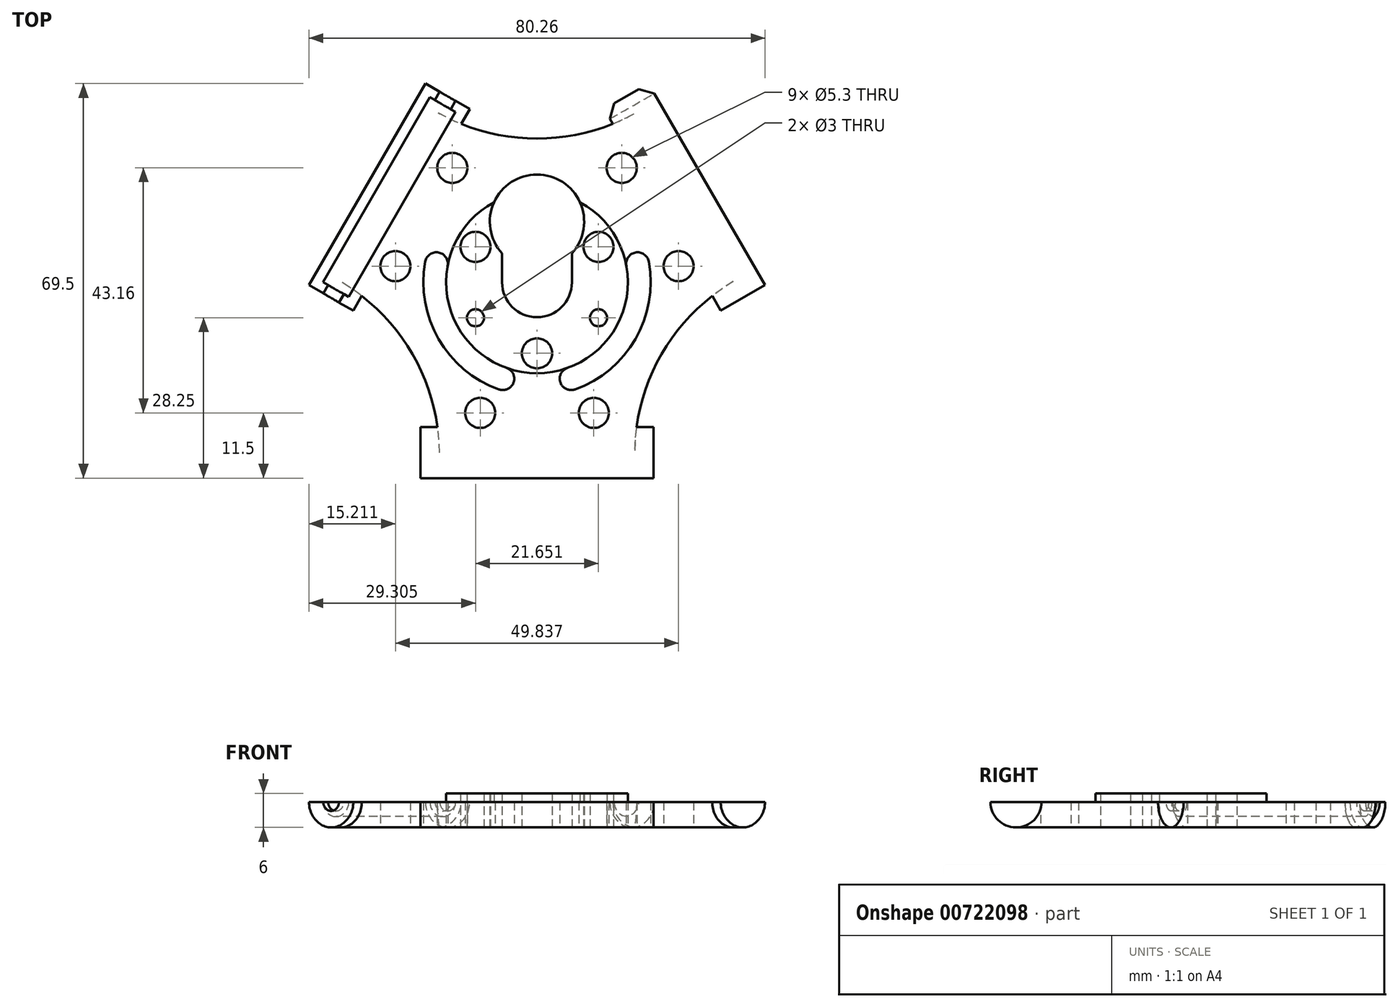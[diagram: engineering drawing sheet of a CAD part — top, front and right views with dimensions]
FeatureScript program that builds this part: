
annotation { "Feature Type Name" : "Feature", "Feature Type Description" : "" }
export const myFeature = defineFeature(function(context is Context, id is Id, definition is map)
    precondition{}
    {
        {
            var Q0;
            Q0=qCreatedBy(makeId("Top.planeOp"),FACE);
            var sketch = newSketch(context, id + "F0", { "sketchPlane" : qUnion([Q0])});
            skArc(sketch, "E0", {"start": v(-6.15, 0) * mm, "mid": v(0, -6.15) * mm, "end": v(6.15, 0) * mm});
            skArc(sketch, "E1", {"start": v(6.15, 5.12) * mm, "mid": v(0, 19) * mm, "end": v(-6.15, 5.12) * mm});
            skLineSegment(sketch, "E2", {"start": v(6.15, 0) * mm, "end": v(6.15, 5.12) * mm});
            skLineSegment(sketch, "E3", {"start": v(-6.15, 0) * mm, "end": v(-6.15, 5.12) * mm});
            skLineSegment(sketch, "E4", {"start": v(-32.33, -5) * mm, "end": v(-30.83, -2.4) * mm});
            skLineSegment(sketch, "E5", {"start": v(-11.83, 30.5) * mm, "end": v(-19.63, 35) * mm});
            skLineSegment(sketch, "E6", {"start": v(-19.63, 35) * mm, "end": v(-40.13, -0.5) * mm});
            skLineSegment(sketch, "E7", {"start": v(-40.13, -0.5) * mm, "end": v(-32.33, -5) * mm});
            skLineSegment(sketch, "E8", {"start": v(-36.23, -2.75) * mm, "end": v(-15.73, 32.75) * mm, "construction": true});
            skLineSegment(sketch, "E9", {"start": v(-25.98, 15) * mm, "end": v(0, 0) * mm, "construction": true});
            skCircle(sketch, "E10", {"center": v(0, 0) * mm, "radius": 8 * mm, "construction": true});
            skLineSegment(sketch, "E11.1.0", {"start": v(20.5, -25.5) * mm, "end": v(17.5, -25.5) * mm});
            skLineSegment(sketch, "E11.1.1", {"start": v(-20.5, -25.5) * mm, "end": v(-20.5, -34.5) * mm});
            skLineSegment(sketch, "E11.1.2", {"start": v(-20.5, -34.5) * mm, "end": v(20.5, -34.5) * mm});
            skLineSegment(sketch, "E11.1.3", {"start": v(20.5, -34.5) * mm, "end": v(20.5, -25.5) * mm});
            skLineSegment(sketch, "E11.1.4", {"start": v(0, -30) * mm, "end": v(0, 0) * mm, "construction": true});
            skLineSegment(sketch, "E11.1.5", {"start": v(20.5, -30) * mm, "end": v(-20.5, -30) * mm, "construction": true});
            skLineSegment(sketch, "E11.2.0", {"start": v(11.83, 30.5) * mm, "end": v(13.33, 27.9) * mm});
            skLineSegment(sketch, "E11.2.1", {"start": v(32.33, -5) * mm, "end": v(40.13, -0.5) * mm});
            skLineSegment(sketch, "E11.2.2", {"start": v(40.13, -0.5) * mm, "end": v(19.63, 35) * mm});
            skLineSegment(sketch, "E11.2.3", {"start": v(19.63, 35) * mm, "end": v(11.83, 30.5) * mm});
            skLineSegment(sketch, "E11.2.4", {"start": v(25.98, 15) * mm, "end": v(0, 0) * mm, "construction": true});
            skLineSegment(sketch, "E11.2.5", {"start": v(15.73, 32.75) * mm, "end": v(36.23, -2.75) * mm, "construction": true});
            skArc(sketch, "E12", {"start": v(-13.33, 27.9) * mm, "mid": v(0, 25.3) * mm, "end": v(13.33, 27.9) * mm});
            skArc(sketch, "E13.1.0", {"start": v(-17.5, -25.5) * mm, "mid": v(-21.92, -12.65) * mm, "end": v(-30.83, -2.4) * mm});
            skArc(sketch, "E13.2.0", {"start": v(30.83, -2.4) * mm, "mid": v(21.92, -12.65) * mm, "end": v(17.5, -25.5) * mm});
            skLineSegment(sketch, "E14.trimOffspring", {"start": v(-13.33, 27.9) * mm, "end": v(-11.83, 30.5) * mm});
            skLineSegment(sketch, "E15.trimOffspring", {"start": v(-17.5, -25.5) * mm, "end": v(-20.5, -25.5) * mm});
            skLineSegment(sketch, "E16.trimOffspring", {"start": v(30.83, -2.4) * mm, "end": v(32.33, -5) * mm});
            skCircle(sketch, "E17", {"center": v(0, -12.5) * mm, "radius": 2.65 * mm});
            skCircle(sketch, "E18.2.0", {"center": v(10.83, 6.25) * mm, "radius": 2.65 * mm});
            skCircle(sketch, "E18.4.0", {"center": v(-10.83, 6.25) * mm, "radius": 2.65 * mm});
            skCircle(sketch, "E18.5.0", {"center": v(-10.83, -6.25) * mm, "radius": 1.5 * mm});
            skCircle(sketch, "E19", {"center": v(-24.92, 2.84) * mm, "radius": 2.65 * mm});
            skCircle(sketch, "E20.MirrorC", {"center": v(-14.92, 20.16) * mm, "radius": 2.65 * mm});
            skArc(sketch, "E21", {"start": v(-15.73, 2.92) * mm, "mid": v(-13.86, -8) * mm, "end": v(-5.33, -15.08) * mm});
            skCircle(sketch, "E22.1.0", {"center": v(10, -23) * mm, "radius": 2.65 * mm});
            skCircle(sketch, "E22.1.1", {"center": v(-10, -23) * mm, "radius": 2.65 * mm});
            skCircle(sketch, "E22.2.0", {"center": v(14.92, 20.16) * mm, "radius": 2.65 * mm});
            skCircle(sketch, "E22.2.1", {"center": v(24.92, 2.84) * mm, "radius": 2.65 * mm});
            skArc(sketch, "E23", {"start": v(-19.66, 3.65) * mm, "mid": v(-17.32, -10) * mm, "end": v(-6.67, -18.86) * mm});
            skArc(sketch, "E24", {"start": v(-15.73, 2.92) * mm, "mid": v(-17.33, 5.26) * mm, "end": v(-19.66, 3.65) * mm});
            skArc(sketch, "E25", {"start": v(-6.67, -18.86) * mm, "mid": v(-4.11, -17.64) * mm, "end": v(-5.33, -15.08) * mm});
            skArc(sketch, "E26.MirrorCS", {"start": v(15.73, 2.92) * mm, "mid": v(13.86, -8) * mm, "end": v(5.33, -15.08) * mm});
            skArc(sketch, "E27.MirrorCS", {"start": v(19.66, 3.65) * mm, "mid": v(17.32, -10) * mm, "end": v(6.67, -18.86) * mm});
            skArc(sketch, "E28.MirrorCS", {"start": v(15.73, 2.92) * mm, "mid": v(17.33, 5.26) * mm, "end": v(19.66, 3.65) * mm});
            skArc(sketch, "E29.MirrorCS", {"start": v(6.67, -18.86) * mm, "mid": v(4.11, -17.64) * mm, "end": v(5.33, -15.08) * mm});
            skLineSegment(sketch, "E30", {"start": v(-10.83, -6.25) * mm, "end": v(0, 0) * mm, "construction": true});
            skCircle(sketch, "E31", {"center": v(0, 0) * mm, "radius": 12.5 * mm, "construction": true});
            skCircle(sketch, "E32.MirrorC", {"center": v(10.83, -6.25) * mm, "radius": 1.5 * mm});
            skSolve(sketch);
        }
        {
            var Q0;
            Q0 = qSketchRegion(id + "F0", true);
            extrude(context, id + "F1", {"entities" : qUnion([Q0]), "depth" : 4.5 * mm, "offsetDistance" : 25 * mm});
        }
        {
            var Q0;
            Q0=makeQuery(id+"F1.opExtrude","SWEPT_FACE",FACE,{"disambiguationData":[OSD([sQuery(id+"F0.wireOp",EDGE,"E7")])]});
            var sketch = newSketch(context, id + "F2", { "sketchPlane" : qUnion([Q0])});
            skCircle(sketch, "E33", {"center": v(-30, 4.5) * mm, "radius": 1.6 * mm});
            skSolve(sketch);
        }
        {
            var Q0;
            Q0 = qSketchRegion(id + "F2", true);
            extrude(context, id + "F3", {"entities" : qUnion([Q0]), "operationType" : NewBodyOperationType.REMOVE, "endBound" : BoundingType.THROUGH_ALL, "oppositeDirection" : true, "depth" : 25 * mm, "offsetDistance" : 25 * mm});
        }
        {
            var Q0;
            Q0=makeQuery(id+"F1.opExtrude","SWEPT_FACE",FACE,{"disambiguationData":[OSD([sQuery(id+"F0.wireOp",EDGE,"E7")])]});
            var Q1;
            Q1=qCreatedBy(makeId("Origin.pointOp"),VERTEX);
            cPlane(context, id + "F4", {"entities" : qUnion([Q0, Q1]), "cplaneType" : CPlaneType.PLANE_POINT, "offset" : 25 * mm, "width" : 150 * mm, "height" : 150 * mm});
        }
        {
            var Q0;
            Q0=qCreatedBy(id+"F4.planeOp",FACE);
            var sketch = newSketch(context, id + "F5", { "sketchPlane" : qUnion([Q0])});
            skArc(sketch, "E34", {"start": v(-31.6, 4.5) * mm, "mid": v(-30, 2.9) * mm, "end": v(-28.4, 4.5) * mm, "construction": true});
            skCircle(sketch, "E35", {"center": v(-30, 4.5) * mm, "radius": 2.6 * mm});
            skSolve(sketch);
        }
        {
            var Q0;
            Q0 = qSketchRegion(id + "F5", true);
            extrude(context, id + "F6", {"entities" : qUnion([Q0]), "operationType" : NewBodyOperationType.REMOVE, "oppositeDirection" : true, "depth" : 18.8 * mm, "offsetDistance" : 25 * mm, "hasSecondDirection" : true, "secondDirectionOppositeDirection" : false, "secondDirectionDepth" : 18.8 * mm});
        }
        {
            var Q0;
            Q0=qCreatedBy(makeId("Front.planeOp"),FACE);
            var sketch = newSketch(context, id + "F7", { "sketchPlane" : qUnion([Q0])});
            skLineSegment(sketch, "E36", {"start": v(0, 0) * mm, "end": v(0, 59.84) * mm, "construction": true});
            skSolve(sketch);
        }
        {
            var Q0;
            Q0=makeQuery(id+"F1.opExtrude","CAP_EDGE",EDGE,{"disambiguationData":[OSD([sQuery(id+"F0.wireOp",EDGE,"E4")])],"isStart":true});
            var Q1;
            Q1=makeQuery(id+"F1.opExtrude","CAP_EDGE",EDGE,{"disambiguationData":[OSD([sQuery(id+"F0.wireOp",EDGE,"E6")])],"isStart":true});
            var Q2;
            Q2=makeQuery(id+"F1.opExtrude","CAP_EDGE",EDGE,{"disambiguationData":[OSD([sQuery(id+"F0.wireOp",EDGE,"E14.trimOffspring")])],"isStart":true});
            var Q3;
            Q3=makeQuery(id+"F1.opExtrude","CAP_EDGE",EDGE,{"disambiguationData":[OSD([sQuery(id+"F0.wireOp",EDGE,"E15.trimOffspring")])],"isStart":true});
            var Q4;
            Q4=makeQuery(id+"F1.opExtrude","CAP_EDGE",EDGE,{"disambiguationData":[OSD([sQuery(id+"F0.wireOp",EDGE,"E11.1.2")])],"isStart":true});
            var Q5;
            Q5=makeQuery(id+"F1.opExtrude","CAP_EDGE",EDGE,{"disambiguationData":[OSD([sQuery(id+"F0.wireOp",EDGE,"E11.1.0")])],"isStart":true});
            var Q6;
            Q6=makeQuery(id+"F1.opExtrude","CAP_EDGE",EDGE,{"disambiguationData":[OSD([sQuery(id+"F0.wireOp",EDGE,"E16.trimOffspring")])],"isStart":true});
            var Q7;
            Q7=makeQuery(id+"F1.opExtrude","CAP_EDGE",EDGE,{"disambiguationData":[OSD([sQuery(id+"F0.wireOp",EDGE,"E11.2.2")])],"isStart":true});
            var Q8;
            Q8=makeQuery(id+"F1.opExtrude","CAP_EDGE",EDGE,{"disambiguationData":[OSD([sQuery(id+"F0.wireOp",EDGE,"E11.2.0")])],"isStart":true});
            fillet(context, id + "F8", {"entities" : qUnion([Q0, Q1, Q2, Q3, Q4, Q5, Q6, Q7, Q8]), "radius" : 4.5 * mm, "tangentPropagation" : true, "allowEdgeOverflow" : false});
        }
        {
            var Q0;
            Q0=makeQuery(id+"F8.opFillet","BLEND_EDGE",EDGE,{"blendedFrom":[makeQuery(id+"F1.opExtrude","CAP_EDGE",EDGE,{"disambiguationData":[OSD([sQuery(id+"F0.wireOp",EDGE,"E6")])],"isStart":true}),makeQuery(id+"F1.opExtrude","SWEPT_FACE",FACE,{"disambiguationData":[OSD([sQuery(id+"F0.wireOp",EDGE,"E7")])]})],"blendedInto":[makeQuery(id+"F1.opExtrude","SWEPT_FACE",FACE,{"disambiguationData":[OSD([sQuery(id+"F0.wireOp",EDGE,"E7")])]})]});
            var Q1;
            Q1=makeQuery(id+"F8.opFillet","BLEND_EDGE",EDGE,{"blendedFrom":[makeQuery(id+"F1.opExtrude","CAP_EDGE",EDGE,{"disambiguationData":[OSD([sQuery(id+"F0.wireOp",EDGE,"E14.trimOffspring")])],"isStart":true}),makeQuery(id+"F1.opExtrude","SWEPT_FACE",FACE,{"disambiguationData":[OSD([sQuery(id+"F0.wireOp",EDGE,"E5")])]})],"blendedInto":[makeQuery(id+"F1.opExtrude","SWEPT_FACE",FACE,{"disambiguationData":[OSD([sQuery(id+"F0.wireOp",EDGE,"E5")])]})]});
            var Q2;
            Q2=makeQuery(id+"F8.opFillet","BLEND_EDGE",EDGE,{"blendedFrom":[makeQuery(id+"F1.opExtrude","CAP_EDGE",EDGE,{"disambiguationData":[OSD([sQuery(id+"F0.wireOp",EDGE,"E11.2.0")])],"isStart":true}),makeQuery(id+"F1.opExtrude","SWEPT_FACE",FACE,{"disambiguationData":[OSD([sQuery(id+"F0.wireOp",EDGE,"E11.2.3")])]})],"blendedInto":[makeQuery(id+"F1.opExtrude","SWEPT_FACE",FACE,{"disambiguationData":[OSD([sQuery(id+"F0.wireOp",EDGE,"E11.2.3")])]})]});
            var Q3;
            Q3=makeQuery(id+"F8.opFillet","BLEND_EDGE",EDGE,{"blendedFrom":[makeQuery(id+"F1.opExtrude","CAP_EDGE",EDGE,{"disambiguationData":[OSD([sQuery(id+"F0.wireOp",EDGE,"E15.trimOffspring")])],"isStart":true}),makeQuery(id+"F1.opExtrude","SWEPT_FACE",FACE,{"disambiguationData":[OSD([sQuery(id+"F0.wireOp",EDGE,"E11.1.1")])]})],"blendedInto":[makeQuery(id+"F1.opExtrude","SWEPT_FACE",FACE,{"disambiguationData":[OSD([sQuery(id+"F0.wireOp",EDGE,"E11.1.1")])]})]});
            var Q4;
            Q4=makeQuery(id+"F8.opFillet","BLEND_EDGE",EDGE,{"blendedFrom":[makeQuery(id+"F1.opExtrude","CAP_EDGE",EDGE,{"disambiguationData":[OSD([sQuery(id+"F0.wireOp",EDGE,"E11.1.2")])],"isStart":true}),makeQuery(id+"F1.opExtrude","SWEPT_FACE",FACE,{"disambiguationData":[OSD([sQuery(id+"F0.wireOp",EDGE,"E11.1.3")])]})],"blendedInto":[makeQuery(id+"F1.opExtrude","SWEPT_FACE",FACE,{"disambiguationData":[OSD([sQuery(id+"F0.wireOp",EDGE,"E11.1.3")])]})]});
            var Q5;
            Q5=makeQuery(id+"F8.opFillet","BLEND_EDGE",EDGE,{"blendedFrom":[makeQuery(id+"F1.opExtrude","CAP_EDGE",EDGE,{"disambiguationData":[OSD([sQuery(id+"F0.wireOp",EDGE,"E16.trimOffspring")])],"isStart":true}),makeQuery(id+"F1.opExtrude","SWEPT_FACE",FACE,{"disambiguationData":[OSD([sQuery(id+"F0.wireOp",EDGE,"E11.2.1")])]})],"blendedInto":[makeQuery(id+"F1.opExtrude","SWEPT_FACE",FACE,{"disambiguationData":[OSD([sQuery(id+"F0.wireOp",EDGE,"E11.2.1")])]})]});
            chamfer(context, id + "F9", {"entities" : qUnion([Q0, Q1, Q2, Q3, Q4, Q5]), "width" : 2 * mm, "tangentPropagation" : true});
        }
        {
            var Q0;
            {var subQ0=sQuery(id+"F0.wireOp",EDGE,"E29.MirrorCS");var subQ2=sQuery(id+"F0.wireOp",EDGE,"E28.MirrorCS");var subQ4=sQuery(id+"F0.wireOp",EDGE,"E27.MirrorCS");var subQ8=sQuery(id+"F0.wireOp",EDGE,"E26.MirrorCS");var subQ11=sQuery(id+"F0.wireOp",EDGE,"E25");var subQ14=sQuery(id+"F0.wireOp",EDGE,"E24");var subQ16=sQuery(id+"F0.wireOp",EDGE,"E23");var subQ18=sQuery(id+"F0.wireOp",EDGE,"E22.2.1");var subQ20=sQuery(id+"F0.wireOp",EDGE,"E22.2.0");var subQ22=sQuery(id+"F0.wireOp",EDGE,"E22.1.1");var subQ24=sQuery(id+"F0.wireOp",EDGE,"E22.1.0");var subQ26=sQuery(id+"F0.wireOp",EDGE,"E21");var subQ28=sQuery(id+"F0.wireOp",EDGE,"E20.MirrorC");var subQ30=sQuery(id+"F0.wireOp",EDGE,"E19");var subQ32=sQuery(id+"F0.wireOp",EDGE,"E18.5.0");var subQ34=sQuery(id+"F0.wireOp",EDGE,"E18.4.0");var subQ36=sQuery(id+"F0.wireOp",EDGE,"E11.1.3");var subQ38=sQuery(id+"F0.wireOp",EDGE,"E11.1.0");var subQ40=sQuery(id+"F0.wireOp",EDGE,"E7");var subQ42=sQuery(id+"F0.wireOp",EDGE,"E5");var subQ47=sQuery(id+"F0.wireOp",EDGE,"E17");var subQ49=sQuery(id+"F0.wireOp",EDGE,"E4");var subQ51=sQuery(id+"F0.wireOp",EDGE,"E11.1.1");var subQ53=sQuery(id+"F0.wireOp",EDGE,"E0");var subQ54=makeQuery(id+"F1.opExtrude","SWEPT_FACE",FACE,{"disambiguationData":[OSD([subQ53])]});var subQ55=sQuery(id+"F0.wireOp",EDGE,"E16.trimOffspring");var subQ57=sQuery(id+"F0.wireOp",EDGE,"E3");var subQ59=sQuery(id+"F0.wireOp",EDGE,"E1");var subQ61=sQuery(id+"F0.wireOp",EDGE,"E18.2.0");var subQ63=sQuery(id+"F0.wireOp",EDGE,"E2");var subQ65=sQuery(id+"F0.wireOp",EDGE,"E11.2.0");var subQ67=sQuery(id+"F0.wireOp",EDGE,"E11.2.1");var subQ69=sQuery(id+"F0.wireOp",EDGE,"E11.2.3");var subQ72=sQuery(id+"F0.wireOp",EDGE,"E12");var subQ74=sQuery(id+"F0.wireOp",EDGE,"E13.1.0");var subQ76=sQuery(id+"F0.wireOp",EDGE,"E13.2.0");var subQ78=sQuery(id+"F0.wireOp",EDGE,"E14.trimOffspring");var subQ80=sQuery(id+"F0.wireOp",EDGE,"E15.trimOffspring");var subQ82=sQuery(id+"F0.wireOp",EDGE,"E18.1.0");var subQ84=sQuery(id+"F0.wireOp",EDGE,"E11.2.2");var subQ86=sQuery(id+"F0.wireOp",EDGE,"E11.1.2");Q0=makeQuery(id+"Fxi4iVRiwFdOaLl_1.2.F3.boolean.opBoolean","SPLIT",FACE,{"disambiguationData":[TD([subQ54])],"derivedFrom":makeQuery(id+"Fxi4iVRiwFdOaLl_1.1.F3.boolean.opBoolean","SPLIT",FACE,{"disambiguationData":[TD([subQ54])],"derivedFrom":makeQuery(id+"F3.boolean.opBoolean","SPLIT",FACE,{"disambiguationData":[TD([subQ54])],"derivedFrom":makeQuery(id+"F1.opExtrude","CAP_FACE",FACE,{"disambiguationData":[OSD([subQ53,subQ59,subQ63,subQ57,subQ49,subQ42,sQuery(id+"F0.wireOp",EDGE,"E6"),subQ40,subQ38,subQ51,subQ86,subQ36,subQ65,subQ67,subQ84,subQ69,subQ72,subQ74,subQ76,subQ78,subQ80,subQ55,subQ47,subQ82,subQ61,subQ34,subQ32,subQ30,subQ28,subQ26,subQ24,subQ22,subQ20,subQ18,subQ16,subQ14,subQ11,subQ8,subQ4,subQ2,subQ0])],"isStart":false})})})});}
            var sketch = newSketch(context, id + "F10", { "sketchPlane" : qUnion([Q0])});
            skArc(sketch, "E37", {"start": v(-7.57, 14.1) * mm, "mid": v(0, -16) * mm, "end": v(7.57, 14.1) * mm});
            skArc(sketch, "E38.0", {"start": v(6.15, 5.12) * mm, "mid": v(8.2, 9.4) * mm, "end": v(7.57, 14.1) * mm});
            skLineSegment(sketch, "E39.0", {"start": v(-6.15, 0) * mm, "end": v(-6.15, 5.12) * mm});
            skArc(sketch, "E40.0", {"start": v(-6.15, 0) * mm, "mid": v(0, -6.15) * mm, "end": v(6.15, 0) * mm});
            skLineSegment(sketch, "E41.0", {"start": v(6.15, 0) * mm, "end": v(6.15, 5.12) * mm});
            skCircle(sketch, "E42.0", {"center": v(10.83, 6.25) * mm, "radius": 2.65 * mm});
            skCircle(sketch, "E43.0", {"center": v(0, -12.5) * mm, "radius": 2.65 * mm});
            skCircle(sketch, "E44.0", {"center": v(-10.83, -6.25) * mm, "radius": 1.5 * mm});
            skCircle(sketch, "E45.0", {"center": v(-10.83, 6.25) * mm, "radius": 2.65 * mm});
            skArc(sketch, "E46.trimOffspring", {"start": v(-7.57, 14.1) * mm, "mid": v(-8.2, 9.4) * mm, "end": v(-6.15, 5.12) * mm});
            skCircle(sketch, "E47.0", {"center": v(10.83, -6.25) * mm, "radius": 1.5 * mm});
            skSolve(sketch);
        }
        {
            var Q0;
            Q0 = qSketchRegion(id + "F10", true);
            var Q1;
            Q1=makeQuery(id+"F1.opExtrude","CAP_FACE",FACE,{"disambiguationData":[OSD([sQuery(id+"F0.wireOp",EDGE,"E0"),sQuery(id+"F0.wireOp",EDGE,"E1"),sQuery(id+"F0.wireOp",EDGE,"E2"),sQuery(id+"F0.wireOp",EDGE,"E3"),sQuery(id+"F0.wireOp",EDGE,"E4"),sQuery(id+"F0.wireOp",EDGE,"E5"),sQuery(id+"F0.wireOp",EDGE,"E6"),sQuery(id+"F0.wireOp",EDGE,"E7"),sQuery(id+"F0.wireOp",EDGE,"E11.1.0"),sQuery(id+"F0.wireOp",EDGE,"E11.1.1"),sQuery(id+"F0.wireOp",EDGE,"E11.1.2"),sQuery(id+"F0.wireOp",EDGE,"E11.1.3"),sQuery(id+"F0.wireOp",EDGE,"E11.2.0"),sQuery(id+"F0.wireOp",EDGE,"E11.2.1"),sQuery(id+"F0.wireOp",EDGE,"E11.2.2"),sQuery(id+"F0.wireOp",EDGE,"E11.2.3"),sQuery(id+"F0.wireOp",EDGE,"E12"),sQuery(id+"F0.wireOp",EDGE,"E13.1.0"),sQuery(id+"F0.wireOp",EDGE,"E13.2.0"),sQuery(id+"F0.wireOp",EDGE,"E14.trimOffspring"),sQuery(id+"F0.wireOp",EDGE,"E15.trimOffspring"),sQuery(id+"F0.wireOp",EDGE,"E16.trimOffspring"),sQuery(id+"F0.wireOp",EDGE,"E17"),sQuery(id+"F0.wireOp",EDGE,"E18.1.0"),sQuery(id+"F0.wireOp",EDGE,"E18.2.0"),sQuery(id+"F0.wireOp",EDGE,"E18.4.0"),sQuery(id+"F0.wireOp",EDGE,"E18.5.0"),sQuery(id+"F0.wireOp",EDGE,"E19"),sQuery(id+"F0.wireOp",EDGE,"E20.MirrorC"),sQuery(id+"F0.wireOp",EDGE,"E21"),sQuery(id+"F0.wireOp",EDGE,"E22.1.0"),sQuery(id+"F0.wireOp",EDGE,"E22.1.1"),sQuery(id+"F0.wireOp",EDGE,"E22.2.0"),sQuery(id+"F0.wireOp",EDGE,"E22.2.1"),sQuery(id+"F0.wireOp",EDGE,"E23"),sQuery(id+"F0.wireOp",EDGE,"E24"),sQuery(id+"F0.wireOp",EDGE,"E25"),sQuery(id+"F0.wireOp",EDGE,"E26.MirrorCS"),sQuery(id+"F0.wireOp",EDGE,"E27.MirrorCS"),sQuery(id+"F0.wireOp",EDGE,"E28.MirrorCS"),sQuery(id+"F0.wireOp",EDGE,"E29.MirrorCS")])],"isStart":true});
            extrude(context, id + "F11", {"entities" : qUnion([Q0]), "operationType" : NewBodyOperationType.ADD, "depth" : 1.5 * mm, "endBoundEntityFace" : qUnion([Q1]), "hasOffset" : true, "offsetDistance" : 10 * mm, "offsetOppositeDirection" : true});
        }
    });
